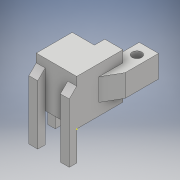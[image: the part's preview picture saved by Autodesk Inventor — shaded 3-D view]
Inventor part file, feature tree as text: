
AUTODESK INVENTOR PART (.ipt)
format: ipt  version: 2018 (Build 220112000, 112)  size: 175,616 bytes
history: native  units: mm
features: sketch x8, extrude x6, draft x3
ambient origin geometry x8: Origin, YZ Plane, XZ Plane, XY Plane, X Axis, Y Axis, Z Axis, Center Point
bodies: Solid1 (feature_tree)
feature tree (17):
  extrude  "Extrusion1"  Depth=30.7mm
  extrude  "Extrusion2"  Depth=7.7mm
  draft  "FaceDraft1"
  extrude  "Extrusion3"  Depth=15.0mm
  extrude  "Extrusion4"  TaperAngle=60.0deg  [1 undecoded]
  draft  "FaceDraft2"
  extrude  "Extrusion5"  Depth=6.45mm
  sketch  "Sketch6"  dims[d14=2.5mm d15=20.0mm d16=0.0mm]
  sketch  "Sketch7"  dims[d17=11.5mm]
  extrude  "Extrusion6"  Depth=20.0mm TaperAngle=0.0deg
  draft  "FaceDraft3"
  sketch  "Sketch1"  dims[d0=27.3mm d1=30.7mm]
  sketch  "Sketch2"  dims[d2=31.3mm d3=0.0mm d4=7.7mm]
  sketch  "Sketch3"  dims[d5=13.0mm d6=15.0mm]
  sketch  "Sketch4"  dims[d7=20.0mm d8=5.0mm d9=0.0mm d10=0.0mm d11=60.0deg]
  sketch  "Sketch5"  dims[d12=6.2mm d13=6.45mm]
  sketch  "Sketch8"  dims[d18=5.0mm d19=7.0mm d20=20.0mm d21=12.0mm d22=0.0mm d23=0.0mm d24=45.0deg d25=15.0mm d26=7.0mm d27=20.0mm d28=0.0mm d29=6.0mm d30=5.0mm d31=6.0mm d32=5.0mm d33=20.0mm d34=25.0mm d35=0.0mm d36=0.0mm d37=45.0deg]
note: 1 required parameter value undecoded (feature->parameter linkage not recoverable at this tier; creation-order binding heuristic only, values carry confidence <= 0.55)
